# Revit family: 1712 Spine Lounge Suite Sofa
name_source: partatom
category: Furniture
revit_build: Autodesk Revit 2017 (Build: 20171027_0315(x64)
units: mm (PartAtom-declared; Revit-internal decimal feet)

## family parameters
Always vertical = Yes
Cut with Voids When Loaded = No
OmniClass Number = 23.40.20.00
OmniClass Title = General Furniture and Specialties
Room Calculation Point = No
Shared = No
Work Plane-Based = No

## types (1)
- 1712 Spine Lounge Suite Sofa
    Cushion = FF Black Leather 88
    Depth = 81 cm
    Description = Spine Lounge Suite Sofa pays respect to the traditions of hand upholstering to which Fredericia built its name on, while offering a modern flavour in its own succinct and simple way.
    Design year = 2012
    Designer = Space Copenhagen
    Frame = FF Black Lacquered horizontal
    Height = 71 cm
    Item No. = 1712
    Legs = FF Black Lacquered vertical
    Manufacturer = Fredericia Furniture
    Model = Spine Lounge Suite Sofa
    Seat Height = 41 cm
    Type Comments = Lounge Collection
    URL = https://www.fredericia.com
    Variation Legs = Available in other kind of wood
    Variations = Avalible with felt gliders
    Variations Frame = Available in other kind of wood
    Variations Upholster = Available in fabric and leather
    Weight = 51kg
    Width = 160 cm

## geometry (parser evidence)
native form markers: Sweep x2
no freeform markers — native parametric forms only
